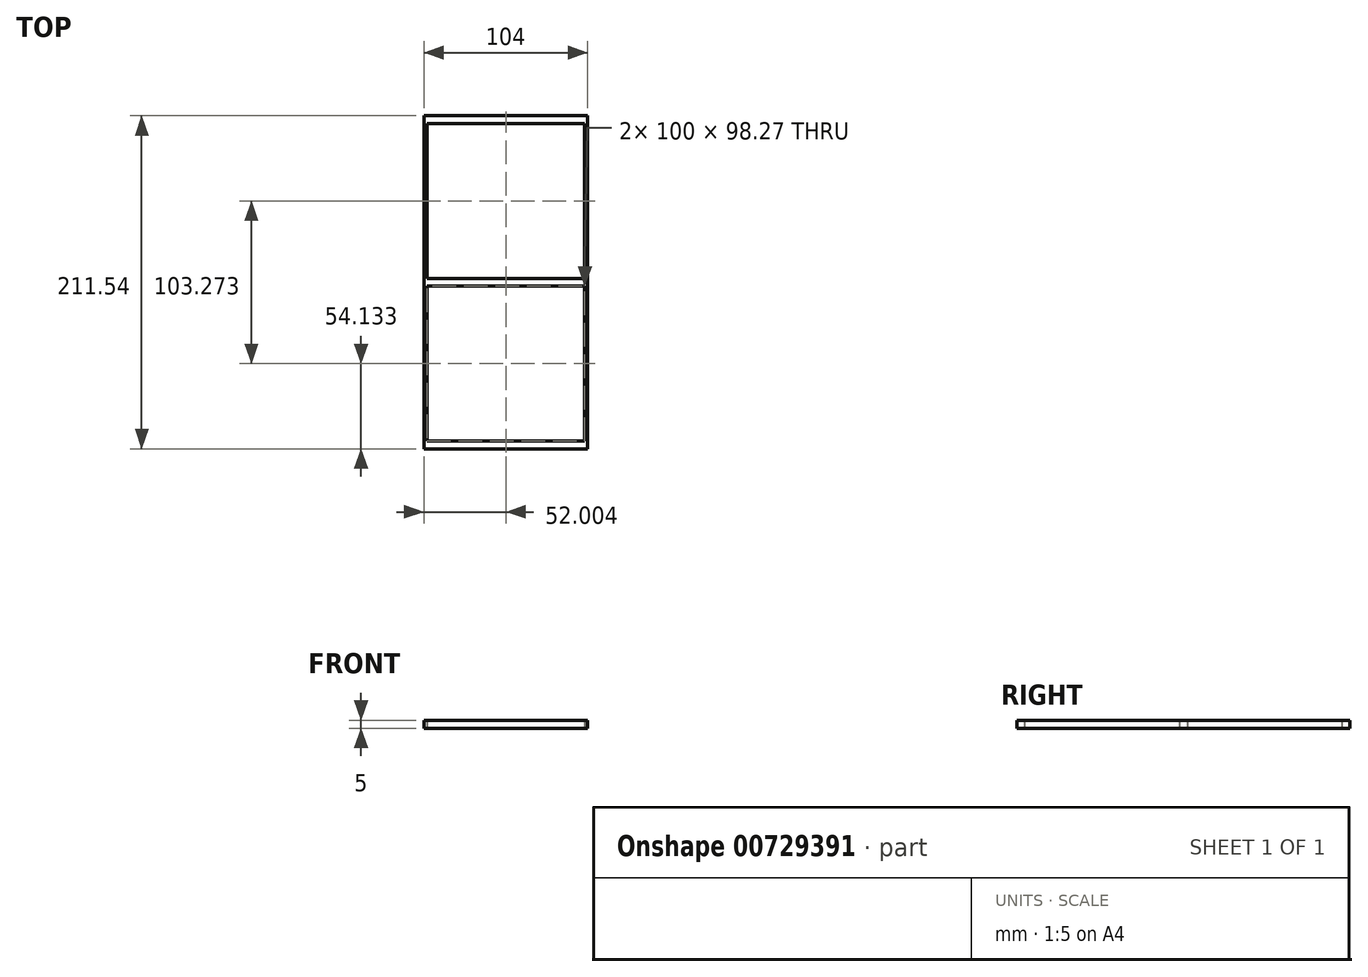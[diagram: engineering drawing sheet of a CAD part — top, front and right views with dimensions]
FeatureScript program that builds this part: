
annotation { "Feature Type Name" : "Feature", "Feature Type Description" : "" }
export const myFeature = defineFeature(function(context is Context, id is Id, definition is map)
    precondition{}
    {
        {
            var Q0;
            Q0=qCreatedBy(makeId("Top.planeOp"),FACE);
            var sketch = newSketch(context, id + "F0", { "sketchPlane" : qUnion([Q0])});
            skLineSegment(sketch, "E0", {"start": v(-35.75, 103.27) * mm, "end": v(64.25, 103.27) * mm});
            skLineSegment(sketch, "E1", {"start": v(-35.75, 103.27) * mm, "end": v(-35.75, -108.27) * mm});
            skLineSegment(sketch, "E2", {"start": v(-35.75, -108.27) * mm, "end": v(64.25, -108.27) * mm});
            skLineSegment(sketch, "E3", {"start": v(64.25, -108.27) * mm, "end": v(64.25, 103.27) * mm});
            skLineSegment(sketch, "E4", {"start": v(-35.75, 98.27) * mm, "end": v(64.25, 98.27) * mm});
            skLineSegment(sketch, "E5", {"start": v(-35.75, -103.27) * mm, "end": v(64.25, -103.27) * mm});
            skLineSegment(sketch, "E6", {"start": v(-35.75, 0) * mm, "end": v(64.25, 0) * mm});
            skLineSegment(sketch, "E7", {"start": v(-35.75, -5) * mm, "end": v(64.25, -5) * mm});
            skPoint(sketch, "E7.endSnap0", {"position": v(64.25, -2.5) * mm});
            skLineSegment(sketch, "E8", {"start": v(-35.75, 103.27) * mm, "end": v(-37.75, 103.27) * mm});
            skLineSegment(sketch, "E9", {"start": v(-37.75, 103.27) * mm, "end": v(-37.75, -108.27) * mm});
            skLineSegment(sketch, "E10", {"start": v(-35.75, -108.27) * mm, "end": v(-37.75, -108.27) * mm});
            skLineSegment(sketch, "E11", {"start": v(64.25, 103.27) * mm, "end": v(66.25, 103.27) * mm});
            skLineSegment(sketch, "E12", {"start": v(66.25, 103.27) * mm, "end": v(66.25, -108.27) * mm});
            skLineSegment(sketch, "E13", {"start": v(66.25, -108.27) * mm, "end": v(64.25, -108.27) * mm});
            skSolve(sketch);
        }
        {
            var Q0;
            {var subQ5=sQuery(id+"F0.wireOp",EDGE,"E8");Q0=makeQuery(id+"F0.imprint","IMPRINT",FACE,{"disambiguationData":[TD([[makeQuery(id+"F0.imprint","IMPRINT",EDGE,{"derivedFrom":subQ5}),1.0]])]});}
            var Q1;
            {var subQ0=sQuery(id+"F0.wireOp",EDGE,"E2");Q1=makeQuery(id+"F0.imprint","IMPRINT",FACE,{"disambiguationData":[TD([[makeQuery(id+"F0.imprint","IMPRINT",EDGE,{"derivedFrom":subQ0}),1.0]])]});}
            var Q2;
            {var subQ0=sQuery(id+"F0.wireOp",EDGE,"E6");Q2=makeQuery(id+"F0.imprint","IMPRINT",FACE,{"disambiguationData":[TD([[makeQuery(id+"F0.imprint","IMPRINT",EDGE,{"derivedFrom":subQ0}),-1.0]])]});}
            var Q3;
            {var subQ0=sQuery(id+"F0.wireOp",EDGE,"E0");Q3=makeQuery(id+"F0.imprint","IMPRINT",FACE,{"disambiguationData":[TD([[makeQuery(id+"F0.imprint","IMPRINT",EDGE,{"derivedFrom":subQ0}),-1.0]])]});}
            var Q4;
            {var subQ6=sQuery(id+"F0.wireOp",EDGE,"E11");Q4=makeQuery(id+"F0.imprint","IMPRINT",FACE,{"disambiguationData":[TD([[makeQuery(id+"F0.imprint","IMPRINT",EDGE,{"derivedFrom":subQ6}),-1.0]])]});}
            extrude(context, id + "F1", {"entities" : qUnion([Q0, Q1, Q2, Q3, Q4]), "depth" : 5 * mm, "offsetDistance" : 25 * mm});
        }
    });
